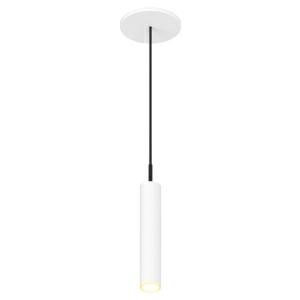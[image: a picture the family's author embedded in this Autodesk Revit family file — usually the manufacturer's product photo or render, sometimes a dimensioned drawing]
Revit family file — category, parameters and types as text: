
# Revit family: hangover_plug_420-2220
name_source: partatom
category: Lighting Fixtures
units: mm (PartAtom-declared; Revit-internal decimal feet)

## family parameters
Cut with Voids When Loaded = No
Host = Face
Light Source = No
Part Type = Normal
Room Calculation Point = No
Round Connector Dimension = Use Diameter
Shared = No

## types (1)
- 420-2220-H27-L00-W22 (1 x LED, 460.09 lm, 6.4 W, 2700K)
    Apparent Load = 6 VA
    CIE Flux Codes = 96 98 99 100 88
    Color Rendering = 1A/90…99
    Color Temperature = 2700K
    Default Elevation = 1800 mm
    Description = HANGOVER PLUG
    Height = 150 mm
    Lamp = 1 x LED
    Lamp Light Flux = 460.09 lm
    Lamp Power = 6.4 W
    Lamp count = 1
    Length = 28 mm
    Luminous efficacy = 63 lm/W
    Manufacturer = Prolicht
    ModVariant = No
    Model = 420-2220
    Mounting Place = Ceiling
    Mounting Type = Pendant
    Number of Poles = 1
    OnlyDefault = Yes
    Power Factor = 1
    Product Name = HANGOVER PLUG
    Product group = Suspended spotlights
    ProductGroupID = 942
    Protection Class = Protection class
    Protection Degree = Degree of protection
    RLX_Detail_Level = 1
    RlxData = <blob elided: 55489 chars, md5=d5a45111>
    Socket = socket
    Standby Power = 0 W
    System Light Flux = 404 lm
    System Power = 6 W
    Type Comments = LED COLOUR DIR 2700 K (27),SHINE RING ABSICHTLICH_LEER (00),BEAMWIDTH Spot (22)
    Type Image = 420-2220.jpg
    URL = http://relux.com
    VarID = 420-2220-h27-l00-w22
    Voltage = 0 V
    Weight = 0.00 kg
    Width = 0 mm  [stored 0 ft]

note: [stored X ft] marks values corroborated as IEEE doubles in the binary element streams (Revit-internal decimal feet)

## geometry (parser evidence)
native form markers: Blend x4, Sweep x11
no freeform markers — native parametric forms only
